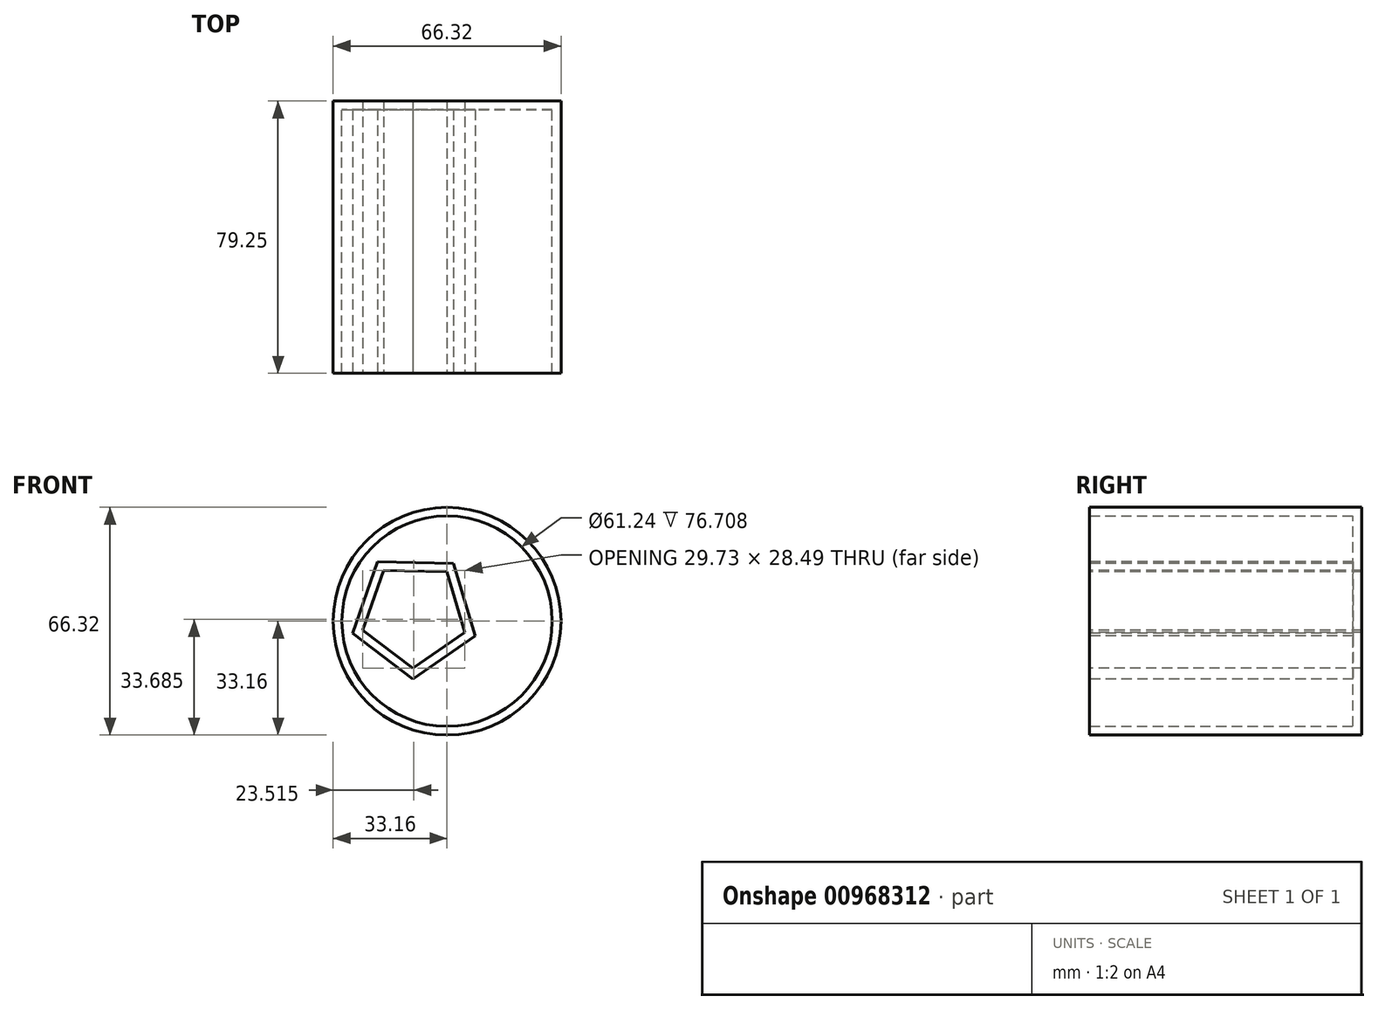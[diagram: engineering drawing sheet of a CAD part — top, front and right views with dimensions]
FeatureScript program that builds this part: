
annotation { "Feature Type Name" : "Feature", "Feature Type Description" : "" }
export const myFeature = defineFeature(function(context is Context, id is Id, definition is map)
    precondition{}
    {
        {
            var Q0;
            Q0=qCreatedBy(makeId("Front.planeOp"),FACE);
            var sketch = newSketch(context, id + "F0", { "sketchPlane" : qUnion([Q0])});
            skCircle(sketch, "E0", {"center": v(0, 0) * mm, "radius": 33.16 * mm});
            skSolve(sketch);
        }
        {
            var Q0;
            Q0 = qSketchRegion(id + "F0", true);
            extrude(context, id + "F1", {"entities" : qUnion([Q0]), "depth" : 79.25 * mm, "offsetDistance" : 25.4 * mm});
        }
        {
            var Q0;
            Q0=makeQuery(id+"F1.opExtrude","CAP_FACE",FACE,{"disambiguationData":[OSD([sQuery(id+"F0.wireOp",EDGE,"E0")])],"isStart":false});
            var sketch = newSketch(context, id + "F2", { "sketchPlane" : qUnion([Q0])});
            skCircle(sketch, "E1.cCircle", {"center": v(-9.53, 1.9) * mm, "radius": 12.65 * mm, "construction": true});
            skLineSegment(sketch, "E1.0", {"start": v(5.22, -3.27) * mm, "end": v(-9.9, -13.72) * mm});
            skLineSegment(sketch, "E1.1", {"start": v(-9.9, -13.72) * mm, "end": v(-24.5, -2.57) * mm});
            skLineSegment(sketch, "E1.2", {"start": v(-24.5, -2.57) * mm, "end": v(-18.42, 14.77) * mm});
            skLineSegment(sketch, "E1.3", {"start": v(-18.42, 14.77) * mm, "end": v(-0.05, 14.34) * mm});
            skLineSegment(sketch, "E1.4", {"start": v(-0.05, 14.34) * mm, "end": v(5.22, -3.27) * mm});
            skPoint(sketch, "E1.0.midPoint", {"position": v(-2.34, -8.5) * mm});
            skSolve(sketch);
        }
        {
            var Q0;
            Q0=makeQuery(id+"F2.imprint","IMPRINT",FACE,{"disambiguationData":[TD([[makeQuery(id+"F2.imprint","IMPRINT",EDGE,{"derivedFrom":sQuery(id+"F2.wireOp",EDGE,"E1.0")}),-1.0]])]});
            extrude(context, id + "F3", {"entities" : qUnion([Q0]), "operationType" : NewBodyOperationType.REMOVE, "oppositeDirection" : true, "depth" : 111.25 * mm, "offsetDistance" : 25.4 * mm});
        }
        {
            var Q0;
            Q0=makeQuery(id+"F1.opExtrude","CAP_FACE",FACE,{"disambiguationData":[OSD([sQuery(id+"F0.wireOp",EDGE,"E0")])],"isStart":false});
            shell(context, id + "F4", {"entities" : qUnion([Q0]), "thickness" : 2.54 * mm});
        }
    });
